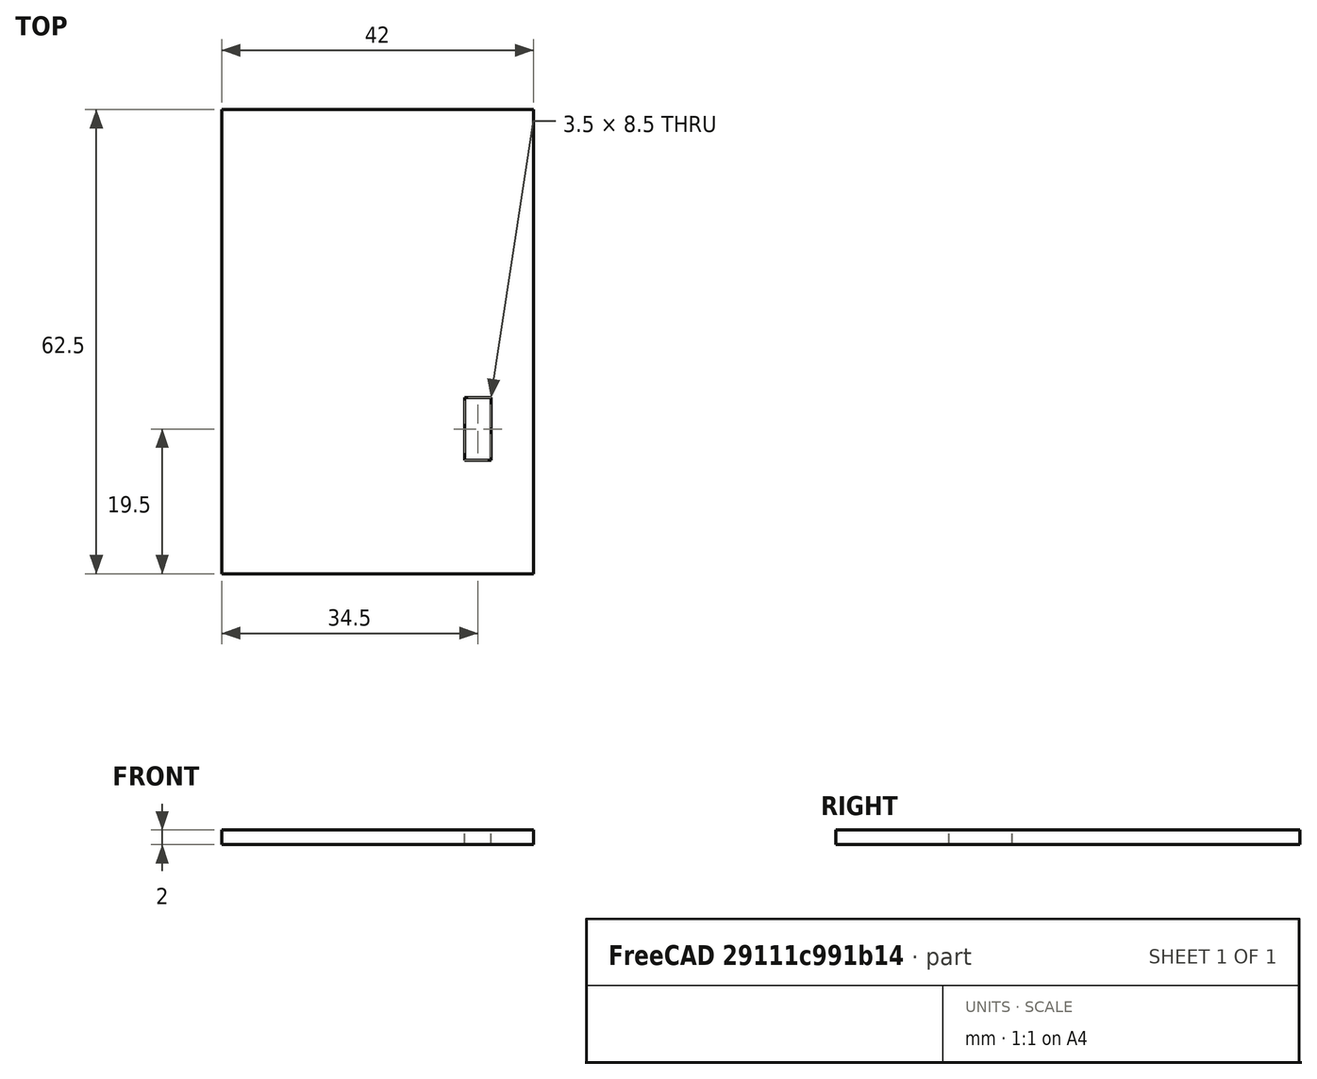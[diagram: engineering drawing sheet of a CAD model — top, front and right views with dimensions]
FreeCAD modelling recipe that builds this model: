
FCSTD DOCUMENT  (FreeCAD 0.19R)
Label: control-board-mount-top
License: All rights reserved
LicenseURL: http://en.wikipedia.org/wiki/All_rights_reserved
objects: Sketcher::SketchObject×1, PartDesign::Pad×1, PartDesign::Body×1, Mesh::Feature×1
note: 4 computed .brp shape members not serialized (recipe doc carries the construction recipe); baked Part::Feature solids carry a one-line shape summary decoded from their .brp

FEATURE [Sketcher::SketchObject] Sketch
  FullyConstrained = true
  MapMode = 5
  Support = -> [XY_Plane]
  sketch-geometry (16):
    g0: LineSegment StartX=0 StartY=0 StartZ=0 EndX=42 EndY=0 EndZ=0
    g1: LineSegment StartX=42 StartY=0 StartZ=0 EndX=42 EndY=62.5 EndZ=0
    g2: LineSegment StartX=42 StartY=62.5 StartZ=0 EndX=0 EndY=62.5 EndZ=0
    g3: LineSegment StartX=0 StartY=62.5 StartZ=0 EndX=0 EndY=0 EndZ=0
    g4: LineSegment StartX=32.75 StartY=23.75 StartZ=0 EndX=36.25 EndY=23.75 EndZ=0
    g5: LineSegment StartX=36.25 StartY=23.75 StartZ=0 EndX=36.25 EndY=15.25 EndZ=0
    g6: LineSegment StartX=36.25 StartY=15.25 StartZ=0 EndX=32.75 EndY=15.25 EndZ=0
    g7: LineSegment StartX=32.75 StartY=15.25 StartZ=0 EndX=32.75 EndY=23.75 EndZ=0
    g8: GeomPoint X=36.25 Y=19.5 Z=0
    g9: GeomPoint X=34.5 Y=15.25 Z=0
    g10: LineSegment StartX=1 StartY=61.5 StartZ=0 EndX=41 EndY=61.5 EndZ=0
    g11: LineSegment StartX=41 StartY=61.5 StartZ=0 EndX=41 EndY=1 EndZ=0
    g12: LineSegment StartX=41 StartY=1 StartZ=0 EndX=1 EndY=1 EndZ=0
    g13: LineSegment StartX=1 StartY=1 StartZ=0 EndX=1 EndY=61.5 EndZ=0
    g14: LineSegment StartX=21 StartY=61.5 StartZ=0 EndX=21 EndY=62.5 EndZ=0
    g15: LineSegment StartX=41 StartY=31.25 StartZ=0 EndX=42 EndY=31.25 EndZ=0
  constraints (41):
    c: Coincident(g0,g1)
    c: Coincident(g1,g2)
    c: Coincident(g2,g3)
    c: Coincident(g3,g0)
    c: Horizontal(g0)
    c: Horizontal(g2)
    c: Vertical(g1)
    c: Vertical(g3)
    c: Coincident(g0,g-1)
    c: Coincident(g4,g5)
    c: Coincident(g5,g6)
    c: Coincident(g6,g7)
    c: Coincident(g7,g4)
    c: Horizontal(g4)
    c: Horizontal(g6)
    c: Vertical(g5)
    c: Vertical(g7)
    c: DistanceX(g2,g2) = 42
    c: DistanceY(g1,g1) = 62.5
    c: Symmetric(g4,g5,g8)
    c: Symmetric(g5,g6,g9)
    c: Coincident(g10,g11)
    c: Coincident(g11,g12)
    c: Coincident(g12,g13)
    c: Coincident(g13,g10)
    c: Horizontal(g10)
    c: Horizontal(g12)
    c: Vertical(g11)
    c: Vertical(g13)
    c: Symmetric(g1,g2,g14)
    c: Symmetric(g10,g10,g14)
    c: Symmetric(g10,g11,g15)
    c: Symmetric(g0,g1,g15)
    c: Vertical(g14)
    c: Horizontal(g15)
    c: DistanceX(g10,g10) = 40
    c: DistanceX(g4,g4) = 3.5
    c: DistanceY(g7,g7) = 8.5
    c: DistanceX(g9,g11) = 6.5
    c: DistanceY(g13,g13) = 60.5
    c: DistanceY(g11,g8) = 18.5
FEATURE [PartDesign::Pad] Pad
  Direction = (1,1,1)
  Length = 2
  Length2 = 100
  Profile = -> Sketch
  Type = 0
FEATURE [PartDesign::Body] Body
  Group = -> [Sketch,Pad]
  Origin = -> Origin
  Tip = -> Pad
FEATURE [Mesh::Feature] Mesh  label="Body (Meshed)"
